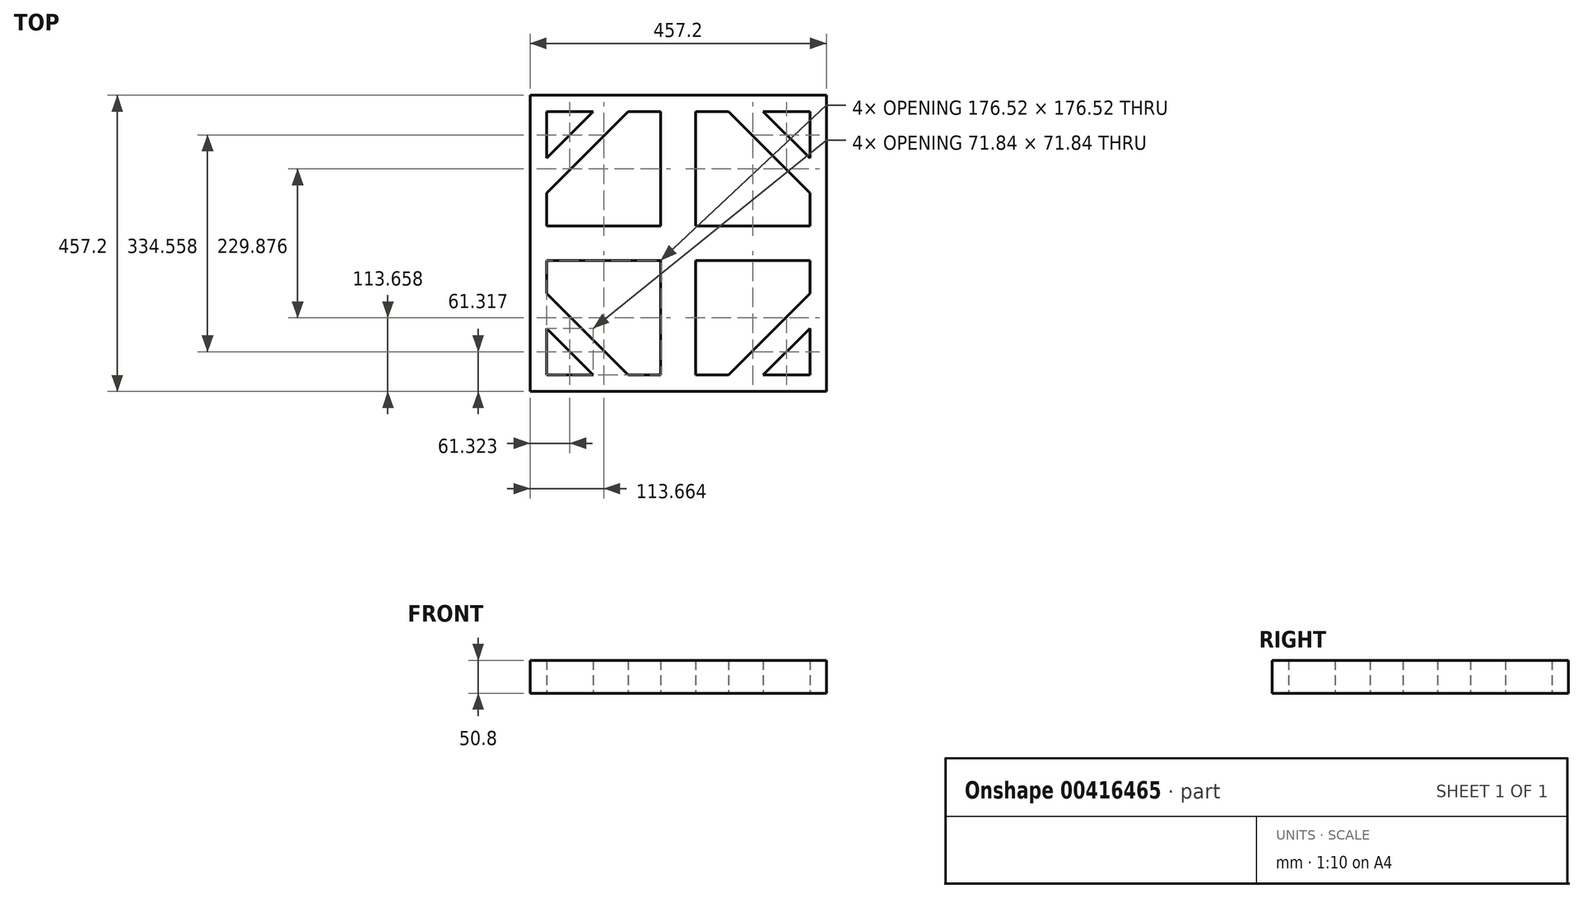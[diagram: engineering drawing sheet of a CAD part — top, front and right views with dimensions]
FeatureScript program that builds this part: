
annotation { "Feature Type Name" : "Feature", "Feature Type Description" : "" }
export const myFeature = defineFeature(function(context is Context, id is Id, definition is map)
    precondition{}
    {
        {
            var Q0;
            Q0=qCreatedBy(makeId("Top.planeOp"),FACE);
            var sketch = newSketch(context, id + "F0", { "sketchPlane" : qUnion([Q0])});
            skLineSegment(sketch, "E0", {"start": v(-227.77, 255.28) * mm, "end": v(229.43, 255.28) * mm});
            skLineSegment(sketch, "E1", {"start": v(-227.77, 255.28) * mm, "end": v(-227.77, -201.92) * mm});
            skLineSegment(sketch, "E2", {"start": v(-227.77, -201.92) * mm, "end": v(229.43, -201.92) * mm});
            skLineSegment(sketch, "E3", {"start": v(229.43, -201.92) * mm, "end": v(229.43, 255.28) * mm});
            skLineSegment(sketch, "E4", {"start": v(-202.37, 229.88) * mm, "end": v(204.03, 229.88) * mm});
            skLineSegment(sketch, "E5", {"start": v(204.03, 229.88) * mm, "end": v(204.03, -176.52) * mm});
            skLineSegment(sketch, "E6", {"start": v(204.03, -176.52) * mm, "end": v(-202.37, -176.52) * mm});
            skLineSegment(sketch, "E7", {"start": v(-202.37, -176.52) * mm, "end": v(-202.37, 229.88) * mm});
            skLineSegment(sketch, "E8", {"start": v(-130.53, 229.88) * mm, "end": v(-202.37, 158.03) * mm});
            skLineSegment(sketch, "E9", {"start": v(132.2, 229.88) * mm, "end": v(204.03, 158.03) * mm});
            skLineSegment(sketch, "E10", {"start": v(-202.37, -104.68) * mm, "end": v(-130.53, -176.52) * mm});
            skLineSegment(sketch, "E11", {"start": v(204.03, -104.68) * mm, "end": v(132.2, -176.52) * mm});
            skLineSegment(sketch, "E12", {"start": v(-227.77, 255.28) * mm, "end": v(-202.37, 229.88) * mm});
            skLineSegment(sketch, "E13", {"start": v(204.03, 229.88) * mm, "end": v(229.43, 255.28) * mm});
            skLineSegment(sketch, "E14", {"start": v(204.03, -176.52) * mm, "end": v(229.43, -201.92) * mm});
            skLineSegment(sketch, "E15", {"start": v(-227.77, -201.92) * mm, "end": v(-202.37, -176.52) * mm});
            skLineSegment(sketch, "E16", {"start": v(-76.64, 229.88) * mm, "end": v(-202.37, 104.15) * mm});
            skLineSegment(sketch, "E17", {"start": v(-202.37, -50.8) * mm, "end": v(-76.64, -176.52) * mm});
            skLineSegment(sketch, "E18", {"start": v(78.3, -176.52) * mm, "end": v(204.03, -50.8) * mm});
            skLineSegment(sketch, "E19", {"start": v(204.03, 104.15) * mm, "end": v(78.3, 229.88) * mm});
            skLineSegment(sketch, "E20", {"start": v(-25.84, 229.88) * mm, "end": v(-25.84, -176.52) * mm});
            skLineSegment(sketch, "E21", {"start": v(27.5, 229.88) * mm, "end": v(27.5, -176.52) * mm});
            skLineSegment(sketch, "E22", {"start": v(-202.37, 53.35) * mm, "end": v(204.03, 53.35) * mm});
            skLineSegment(sketch, "E23", {"start": v(-202.37, 0) * mm, "end": v(204.03, 0) * mm});
            skLineSegment(sketch, "E24", {"start": v(204.03, 0) * mm, "end": v(204.03, -50.8) * mm});
            skLineSegment(sketch, "E25", {"start": v(204.03, 104.15) * mm, "end": v(204.03, 53.35) * mm});
            skLineSegment(sketch, "E26", {"start": v(27.5, -176.52) * mm, "end": v(78.3, -176.52) * mm});
            skLineSegment(sketch, "E27", {"start": v(-25.84, -176.52) * mm, "end": v(-76.64, -176.52) * mm});
            skLineSegment(sketch, "E28", {"start": v(-202.37, 104.15) * mm, "end": v(-202.37, 53.35) * mm});
            skLineSegment(sketch, "E29", {"start": v(-202.37, 0) * mm, "end": v(-202.37, -50.8) * mm});
            skLineSegment(sketch, "E30", {"start": v(-76.64, 229.88) * mm, "end": v(-25.84, 229.88) * mm});
            skLineSegment(sketch, "E31", {"start": v(27.5, 229.88) * mm, "end": v(78.3, 229.88) * mm});
            skLineSegment(sketch, "E32", {"start": v(-202.37, 104.15) * mm, "end": v(-202.37, -50.8) * mm});
            skSolve(sketch);
        }
        {
            var Q0;
            Q0=makeQuery(id+"F0.imprint","IMPRINT",FACE,{"disambiguationData":[TD([[makeQuery(id+"F0.imprint","IMPRINT",EDGE,{"derivedFrom":sQuery(id+"F0.wireOp",EDGE,"E1")}),1.0]])]});
            var Q1;
            Q1=makeQuery(id+"F0.imprint","IMPRINT",FACE,{"disambiguationData":[TD([[makeQuery(id+"F0.imprint","IMPRINT",EDGE,{"derivedFrom":sQuery(id+"F0.wireOp",EDGE,"E2")}),1.0]])]});
            var Q2;
            Q2=makeQuery(id+"F0.imprint","IMPRINT",FACE,{"disambiguationData":[TD([[makeQuery(id+"F0.imprint","IMPRINT",EDGE,{"derivedFrom":sQuery(id+"F0.wireOp",EDGE,"E3")}),1.0]])]});
            var Q3;
            Q3=makeQuery(id+"F0.imprint","IMPRINT",FACE,{"disambiguationData":[TD([[makeQuery(id+"F0.imprint","IMPRINT",EDGE,{"derivedFrom":sQuery(id+"F0.wireOp",EDGE,"E0")}),-1.0]])]});
            extrude(context, id + "F1", {"entities" : qUnion([Q0, Q1, Q2, Q3]), "depth" : 50.8 * mm});
        }
        {
            var Q0;
            {var subQ0=sQuery(id+"F0.wireOp",EDGE,"E8");Q0=makeQuery(id+"F0.imprint","IMPRINT",FACE,{"disambiguationData":[TD([[makeQuery(id+"F0.imprint","IMPRINT",EDGE,{"derivedFrom":subQ0}),1.0]])]});}
            extrude(context, id + "F2", {"entities" : qUnion([Q0]), "operationType" : NewBodyOperationType.REMOVE, "depth" : 50.8 * mm});
        }
        {
            var Q0;
            {var subQ0=sQuery(id+"F0.wireOp",EDGE,"E11");Q0=makeQuery(id+"F0.imprint","IMPRINT",FACE,{"disambiguationData":[TD([[makeQuery(id+"F0.imprint","IMPRINT",EDGE,{"derivedFrom":subQ0}),-1.0]])]});}
            var Q1;
            {var subQ0=sQuery(id+"F0.wireOp",EDGE,"E9");Q1=makeQuery(id+"F0.imprint","IMPRINT",FACE,{"disambiguationData":[TD([[makeQuery(id+"F0.imprint","IMPRINT",EDGE,{"derivedFrom":subQ0}),-1.0]])]});}
            var Q2;
            {var subQ0=sQuery(id+"F0.wireOp",EDGE,"E8");Q2=makeQuery(id+"F0.imprint","IMPRINT",FACE,{"disambiguationData":[TD([[makeQuery(id+"F0.imprint","IMPRINT",EDGE,{"derivedFrom":subQ0}),1.0]])]});}
            var Q3;
            {var subQ0=sQuery(id+"F0.wireOp",EDGE,"E10");Q3=makeQuery(id+"F0.imprint","IMPRINT",FACE,{"disambiguationData":[TD([[makeQuery(id+"F0.imprint","IMPRINT",EDGE,{"derivedFrom":subQ0}),1.0]])]});}
            extrude(context, id + "F3", {"entities" : qUnion([Q0, Q1, Q2, Q3]), "operationType" : NewBodyOperationType.ADD, "depth" : 50.8 * mm});
        }
        {
            var Q0;
            {var subQ0=sQuery(id+"F0.wireOp",EDGE,"E20");var subQ5=sQuery(id+"F0.wireOp",EDGE,"E23");var subQ7=makeQuery(id+"F0.imprint","INTERSECT",VERTEX,{"derivedFrom":[subQ0,subQ5]});Q0=makeQuery(id+"F0.imprint","IMPRINT",FACE,{"disambiguationData":[TD([[makeQuery(id+"F0.imprint","IMPRINT",EDGE,{"disambiguationData":[TD([[subQ7,-1.0]])],"derivedFrom":subQ5}),-1.0]])]});}
            var Q1;
            {var subQ0=sQuery(id+"F0.wireOp",EDGE,"E22");var subQ5=sQuery(id+"F0.wireOp",EDGE,"E21");var subQ6=makeQuery(id+"F0.imprint","INTERSECT",VERTEX,{"derivedFrom":[subQ5,subQ0]});Q1=makeQuery(id+"F0.imprint","IMPRINT",FACE,{"disambiguationData":[TD([[makeQuery(id+"F0.imprint","IMPRINT",EDGE,{"disambiguationData":[TD([[subQ6,-1.0]])],"derivedFrom":subQ5}),1.0]])]});}
            var Q2;
            {var subQ0=sQuery(id+"F0.wireOp",EDGE,"E20");var subQ5=sQuery(id+"F0.wireOp",EDGE,"E22");var subQ6=makeQuery(id+"F0.imprint","INTERSECT",VERTEX,{"derivedFrom":[subQ0,subQ5]});Q2=makeQuery(id+"F0.imprint","IMPRINT",FACE,{"disambiguationData":[TD([[makeQuery(id+"F0.imprint","IMPRINT",EDGE,{"disambiguationData":[TD([[subQ6,-1.0]])],"derivedFrom":subQ5}),1.0]])]});}
            var Q3;
            {var subQ0=sQuery(id+"F0.wireOp",EDGE,"E22");var subQ5=sQuery(id+"F0.wireOp",EDGE,"E20");var subQ6=makeQuery(id+"F0.imprint","INTERSECT",VERTEX,{"derivedFrom":[subQ5,subQ0]});Q3=makeQuery(id+"F0.imprint","IMPRINT",FACE,{"disambiguationData":[TD([[makeQuery(id+"F0.imprint","IMPRINT",EDGE,{"disambiguationData":[TD([[subQ6,-1.0]])],"derivedFrom":subQ5}),-1.0]])]});}
            var Q4;
            {var subQ0=sQuery(id+"F0.wireOp",EDGE,"E22");var subQ1=sQuery(id+"F0.wireOp",EDGE,"E20");var subQ2=makeQuery(id+"F0.imprint","INTERSECT",VERTEX,{"derivedFrom":[subQ1,subQ0]});Q4=makeQuery(id+"F0.imprint","IMPRINT",FACE,{"disambiguationData":[TD([[makeQuery(id+"F0.imprint","IMPRINT",EDGE,{"disambiguationData":[TD([[subQ2,-1.0]])],"derivedFrom":subQ1}),1.0]])]});}
            extrude(context, id + "F4", {"entities" : qUnion([Q0, Q1, Q2, Q3, Q4]), "operationType" : NewBodyOperationType.ADD, "depth" : 50.8 * mm});
        }
    });
